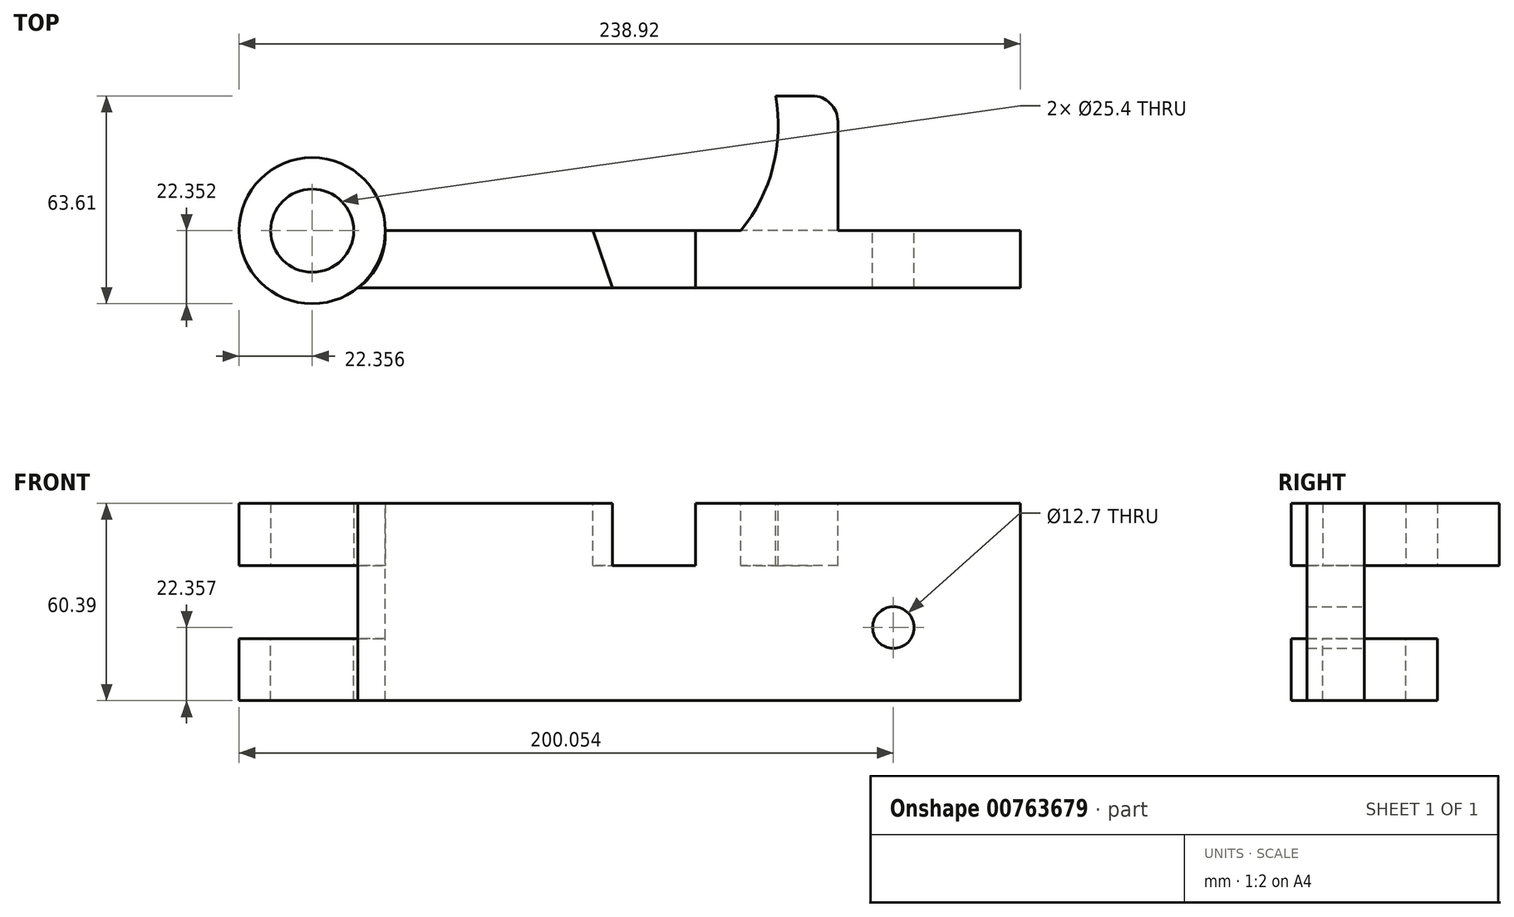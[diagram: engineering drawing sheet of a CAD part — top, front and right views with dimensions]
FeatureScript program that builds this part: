
annotation { "Feature Type Name" : "Feature", "Feature Type Description" : "" }
export const myFeature = defineFeature(function(context is Context, id is Id, definition is map)
    precondition{}
    {
        {
            var Q0;
            Q0=qCreatedBy(makeId("Top.planeOp"),FACE);
            var sketch = newSketch(context, id + "F0", { "sketchPlane" : qUnion([Q0])});
            skLineSegment(sketch, "E0", {"start": v(-24.85, -9.84) * mm, "end": v(191.7, -9.84) * mm});
            skLineSegment(sketch, "E1", {"start": v(191.7, -9.84) * mm, "end": v(191.7, 7.65) * mm});
            skLineSegment(sketch, "E2", {"start": v(191.7, 7.65) * mm, "end": v(-2.5, 7.65) * mm});
            skCircle(sketch, "E3", {"center": v(-24.85, 7.65) * mm, "radius": 22.35 * mm});
            skCircle(sketch, "E4", {"center": v(-24.85, 7.65) * mm, "radius": 12.7 * mm});
            skLineSegment(sketch, "E5", {"start": v(-24.85, 7.65) * mm, "end": v(61, 7.65) * mm, "construction": true});
            skLineSegment(sketch, "E6", {"start": v(-24.85, -9.84) * mm, "end": v(67, -9.84) * mm, "construction": true});
            skLineSegment(sketch, "E7", {"start": v(-24.85, -9.84) * mm, "end": v(92.4, -9.84) * mm, "construction": true});
            skLineSegment(sketch, "E8", {"start": v(-24.85, 7.65) * mm, "end": v(106.18, 7.65) * mm, "construction": true});
            skLineSegment(sketch, "E9", {"start": v(-24.85, 7.65) * mm, "end": v(125.23, 7.65) * mm, "construction": true});
            skLineSegment(sketch, "E10", {"start": v(61, 7.65) * mm, "end": v(67, -9.84) * mm});
            skLineSegment(sketch, "E11", {"start": v(92.4, -9.84) * mm, "end": v(92.4, 7.65) * mm});
            skLineSegment(sketch, "E12", {"start": v(125.23, -9.84) * mm, "end": v(125.23, 7.65) * mm, "construction": true});
            skArc(sketch, "E13", {"start": v(106.18, 7.65) * mm, "mid": v(116.03, 27.11) * mm, "end": v(116.8, 48.9) * mm});
            skLineSegment(sketch, "E14", {"start": v(116.8, 48.9) * mm, "end": v(135.86, 48.9) * mm});
            skLineSegment(sketch, "E15", {"start": v(135.86, 48.9) * mm, "end": v(135.86, 7.65) * mm});
            skSolve(sketch);
        }
        {
            var Q0;
            {var subQ0=sQuery(id+"F0.wireOp",EDGE,"E10");Q0=makeQuery(id+"F0.imprint","IMPRINT",FACE,{"disambiguationData":[TD([[makeQuery(id+"F0.imprint","IMPRINT",EDGE,{"derivedFrom":subQ0}),-1.0]])]});}
            var Q1;
            {var subQ3=sQuery(id+"F0.wireOp",EDGE,"E1");Q1=makeQuery(id+"F0.imprint","IMPRINT",FACE,{"disambiguationData":[TD([[makeQuery(id+"F0.imprint","IMPRINT",EDGE,{"derivedFrom":subQ3}),1.0]])]});}
            var Q2;
            Q2=makeQuery(id+"F0.imprint","IMPRINT",FACE,{"disambiguationData":[TD([[makeQuery(id+"F0.imprint","IMPRINT",EDGE,{"derivedFrom":sQuery(id+"F0.wireOp",EDGE,"E4")}),-1.0]])]});
            var Q3;
            {var subQ0=sQuery(id+"F0.wireOp",EDGE,"E10");Q3=makeQuery(id+"F0.imprint","IMPRINT",FACE,{"disambiguationData":[TD([[makeQuery(id+"F0.imprint","IMPRINT",EDGE,{"derivedFrom":subQ0}),1.0]])]});}
            extrude(context, id + "F1", {"entities" : qUnion([Q0, Q1, Q2, Q3]), "oppositeDirection" : true, "depth" : 60.32 * mm, "offsetDistance" : 25.4 * mm});
        }
        {
            var Q0;
            {var subQ0=sQuery(id+"F0.wireOp",EDGE,"NBQVSlJ4-Jr3w-odm2-qyBv-iB7rYOZyANZf");Q0=makeQuery(id+"F0.imprint","IMPRINT",FACE,{"disambiguationData":[TD([[makeQuery(id+"F0.imprint","IMPRINT",EDGE,{"derivedFrom":subQ0}),1.0]])]});}
            var Q1;
            {var subQ0=sQuery(id+"F0.wireOp",EDGE,"E13");Q1=makeQuery(id+"F0.imprint","IMPRINT",FACE,{"disambiguationData":[TD([[makeQuery(id+"F0.imprint","IMPRINT",EDGE,{"derivedFrom":subQ0}),-1.0]])]});}
            extrude(context, id + "F2", {"entities" : qUnion([Q0, Q1]), "operationType" : NewBodyOperationType.ADD, "oppositeDirection" : true, "depth" : 19.05 * mm, "offsetDistance" : 25.4 * mm});
        }
        {
            var Q0;
            Q0=makeQuery(id+"F2.opExtrude","SWEPT_EDGE",EDGE,{"disambiguationData":[OSD([sQuery(id+"F0.wireOp",EDGE,"E14"),sQuery(id+"F0.wireOp",EDGE,"E15")])]});
            fillet(context, id + "F3", {"entities" : qUnion([Q0]), "radius" : 7.87 * mm, "tangentPropagation" : true, "allowEdgeOverflow" : false});
        }
        {
            var Q0;
            {var subQ0=sQuery(id+"F0.wireOp",EDGE,"E10");Q0=makeQuery(id+"F0.imprint","IMPRINT",FACE,{"disambiguationData":[TD([[makeQuery(id+"F0.imprint","IMPRINT",EDGE,{"derivedFrom":subQ0}),1.0]])]});}
            extrude(context, id + "F4", {"entities" : qUnion([Q0]), "operationType" : NewBodyOperationType.REMOVE, "oppositeDirection" : true, "depth" : 19.05 * mm, "offsetDistance" : 25.4 * mm});
        }
        {
            var Q0;
            Q0=makeQuery(id+"F1.opExtrude","SWEPT_FACE",FACE,{"disambiguationData":[OSD([sQuery(id+"F0.wireOp",EDGE,"E2")])]});
            var sketch = newSketch(context, id + "F5", { "sketchPlane" : qUnion([Q0])});
            skLineSegment(sketch, "E16", {"start": v(-159.2, -37.97) * mm, "end": v(-152.84, -37.97) * mm, "construction": true});
            skCircle(sketch, "E17", {"center": v(-152.84, -37.97) * mm, "radius": 6.35 * mm});
            skLineSegment(sketch, "E18", {"start": v(-11.4, -60.33) * mm, "end": v(-11.4, -41.33) * mm, "construction": true});
            skLineSegment(sketch, "E19", {"start": v(-11.4, 0) * mm, "end": v(-11.4, -19) * mm, "construction": true});
            skLineSegment(sketch, "E20", {"start": v(-11.4, -19) * mm, "end": v(47.42, -19) * mm, "construction": true});
            skLineSegment(sketch, "E21", {"start": v(47.42, -19) * mm, "end": v(-11.4, -19) * mm, "construction": true});
            skLineSegment(sketch, "E22", {"start": v(-11.4, -41.33) * mm, "end": v(53.1, -41.33) * mm, "construction": true});
            skSolve(sketch);
        }
        {
            var Q0;
            Q0=makeQuery(id+"F5.imprint","IMPRINT",FACE,{"disambiguationData":[TD([[makeQuery(id+"F5.imprint","IMPRINT",EDGE,{"derivedFrom":sQuery(id+"F5.wireOp",EDGE,"E17")}),1.0]])]});
            extrude(context, id + "F6", {"entities" : qUnion([Q0]), "operationType" : NewBodyOperationType.REMOVE, "endBound" : BoundingType.THROUGH_ALL, "oppositeDirection" : true, "depth" : 93.22 * mm, "offsetDistance" : 25.4 * mm});
        }
        {
            var Q0;
            {var subQ0=sQuery(id+"F0.wireOp",EDGE,"E4");var subQ1=sQuery(id+"F0.wireOp",EDGE,"E2");var subQ2=sQuery(id+"F0.wireOp",EDGE,"E3");var subQ3=sQuery(id+"F0.wireOp",EDGE,"E0");Q0=makeQuery(id+"F4.boolean.opBoolean","SPLIT",FACE,{"disambiguationData":[TD([makeQuery(id+"F1.opExtrude","SWEPT_FACE",FACE,{"disambiguationData":[OSD([subQ2])]})])],"derivedFrom":makeQuery(id+"F2.boolean.opBoolean","MERGE",FACE,{"derivedFrom":[makeQuery(id+"F1.opExtrude","CAP_FACE",FACE,{"disambiguationData":[OSD([subQ3,sQuery(id+"F0.wireOp",EDGE,"E1"),subQ1,subQ2,subQ0])],"isStart":true}),makeQuery(id+"F2.opExtrude","CAP_FACE",FACE,{"disambiguationData":[OSD([subQ1,sQuery(id+"F0.wireOp",EDGE,"E13"),sQuery(id+"F0.wireOp",EDGE,"E14"),sQuery(id+"F0.wireOp",EDGE,"E15")])],"isStart":true})]})});}
            cPlane(context, id + "F7", {"entities" : qUnion([Q0]), "cplaneType" : CPlaneType.OFFSET, "offset" : 30.16 * mm, "oppositeDirection" : true, "width" : 152.4 * mm, "height" : 152.4 * mm});
        }
        {
            var Q0;
            Q0=qCreatedBy(id+"F7.planeOp",FACE);
            var sketch = newSketch(context, id + "F8", { "sketchPlane" : qUnion([Q0])});
            skLineSegment(sketch, "E23", {"start": v(-24.85, -9.84) * mm, "end": v(191.7, -9.84) * mm});
            skLineSegment(sketch, "E24", {"start": v(191.7, -9.84) * mm, "end": v(191.7, 7.65) * mm});
            skLineSegment(sketch, "E25", {"start": v(191.7, 7.65) * mm, "end": v(-2.5, 7.65) * mm});
            skCircle(sketch, "E26", {"center": v(-24.85, 7.65) * mm, "radius": 22.35 * mm});
            skCircle(sketch, "E27", {"center": v(-24.85, 7.65) * mm, "radius": 12.7 * mm});
            skLineSegment(sketch, "E28", {"start": v(-24.85, 7.65) * mm, "end": v(61, 7.65) * mm, "construction": true});
            skLineSegment(sketch, "E29", {"start": v(-24.85, -9.84) * mm, "end": v(67, -9.84) * mm, "construction": true});
            skLineSegment(sketch, "E30", {"start": v(-24.85, -9.84) * mm, "end": v(92.4, -9.84) * mm, "construction": true});
            skLineSegment(sketch, "E31", {"start": v(-24.85, 7.65) * mm, "end": v(106.18, 7.65) * mm, "construction": true});
            skLineSegment(sketch, "E32", {"start": v(-24.85, 7.65) * mm, "end": v(125.23, 7.65) * mm, "construction": true});
            skLineSegment(sketch, "E33", {"start": v(61, 7.65) * mm, "end": v(67, -9.84) * mm});
            skLineSegment(sketch, "E34", {"start": v(92.4, -9.84) * mm, "end": v(92.4, 7.65) * mm});
            skLineSegment(sketch, "E35", {"start": v(125.23, -9.84) * mm, "end": v(125.23, 7.65) * mm, "construction": true});
            skArc(sketch, "E36", {"start": v(106.18, 7.65) * mm, "mid": v(116.03, 27.11) * mm, "end": v(116.8, 48.9) * mm});
            skLineSegment(sketch, "E37", {"start": v(116.8, 48.9) * mm, "end": v(135.86, 48.9) * mm});
            skLineSegment(sketch, "E38", {"start": v(135.86, 48.9) * mm, "end": v(135.86, 7.65) * mm});
            skSolve(sketch);
        }
        {
            var Q0;
            {var subQ0=sQuery(id+"F0.wireOp",EDGE,"E4");var subQ1=sQuery(id+"F0.wireOp",EDGE,"E2");var subQ2=sQuery(id+"F0.wireOp",EDGE,"E3");var subQ3=sQuery(id+"F0.wireOp",EDGE,"E0");Q0=makeQuery(id+"F4.boolean.opBoolean","SPLIT",FACE,{"disambiguationData":[TD([makeQuery(id+"F1.opExtrude","SWEPT_FACE",FACE,{"disambiguationData":[OSD([subQ2])]})])],"derivedFrom":makeQuery(id+"F2.boolean.opBoolean","MERGE",FACE,{"derivedFrom":[makeQuery(id+"F1.opExtrude","CAP_FACE",FACE,{"disambiguationData":[OSD([subQ3,sQuery(id+"F0.wireOp",EDGE,"E1"),subQ1,subQ2,subQ0])],"isStart":true}),makeQuery(id+"F2.opExtrude","CAP_FACE",FACE,{"disambiguationData":[OSD([subQ1,sQuery(id+"F0.wireOp",EDGE,"E13"),sQuery(id+"F0.wireOp",EDGE,"E14"),sQuery(id+"F0.wireOp",EDGE,"E15")])],"isStart":true})]})});}
            var sketch = newSketch(context, id + "F9", { "sketchPlane" : qUnion([Q0])});
            skArc(sketch, "E39", {"start": v(-10.94, -9.84) * mm, "mid": v(-4.43, -2.2) * mm, "end": v(-2.5, 7.65) * mm});
            skArc(sketch, "E40", {"start": v(10.7, -45.53) * mm, "mid": v(11.6, -38.26) * mm, "end": v(4.43, -39.82) * mm});
            skSolve(sketch);
        }
        {
            var Q0;
            Q0=makeQuery(id+"F9.imprint","IMPRINT",FACE,{"disambiguationData":[TD([[makeQuery(id+"F9.imprint","IMPRINT",EDGE,{"derivedFrom":sQuery(id+"F9.wireOp",EDGE,"E39")}),1.0]])]});
            extrude(context, id + "F10", {"entities" : qUnion([Q0]), "operationType" : NewBodyOperationType.REMOVE, "oppositeDirection" : true, "depth" : 41.4 * mm, "offsetDistance" : 25.4 * mm});
        }
        {
            var Q0;
            Q0=makeQuery(id+"F8.imprint","IMPRINT",FACE,{"disambiguationData":[TD([[makeQuery(id+"F8.imprint","IMPRINT",EDGE,{"derivedFrom":sQuery(id+"F8.wireOp",EDGE,"E27")}),-1.0]])]});
            extrude(context, id + "F11", {"entities" : qUnion([Q0]), "depth" : 30.23 * mm, "offsetDistance" : 25.4 * mm});
        }
        {
            var Q0;
            Q0=makeQuery(id+"F11.opExtrude","CAP_FACE",FACE,{"disambiguationData":[OSD([sQuery(id+"F8.wireOp",EDGE,"E26"),sQuery(id+"F8.wireOp",EDGE,"E27")])],"isStart":true});
            extrude(context, id + "F12", {"entities" : qUnion([Q0]), "operationType" : NewBodyOperationType.REMOVE, "oppositeDirection" : true, "depth" : 11.18 * mm, "offsetDistance" : 25.4 * mm});
        }
    });
